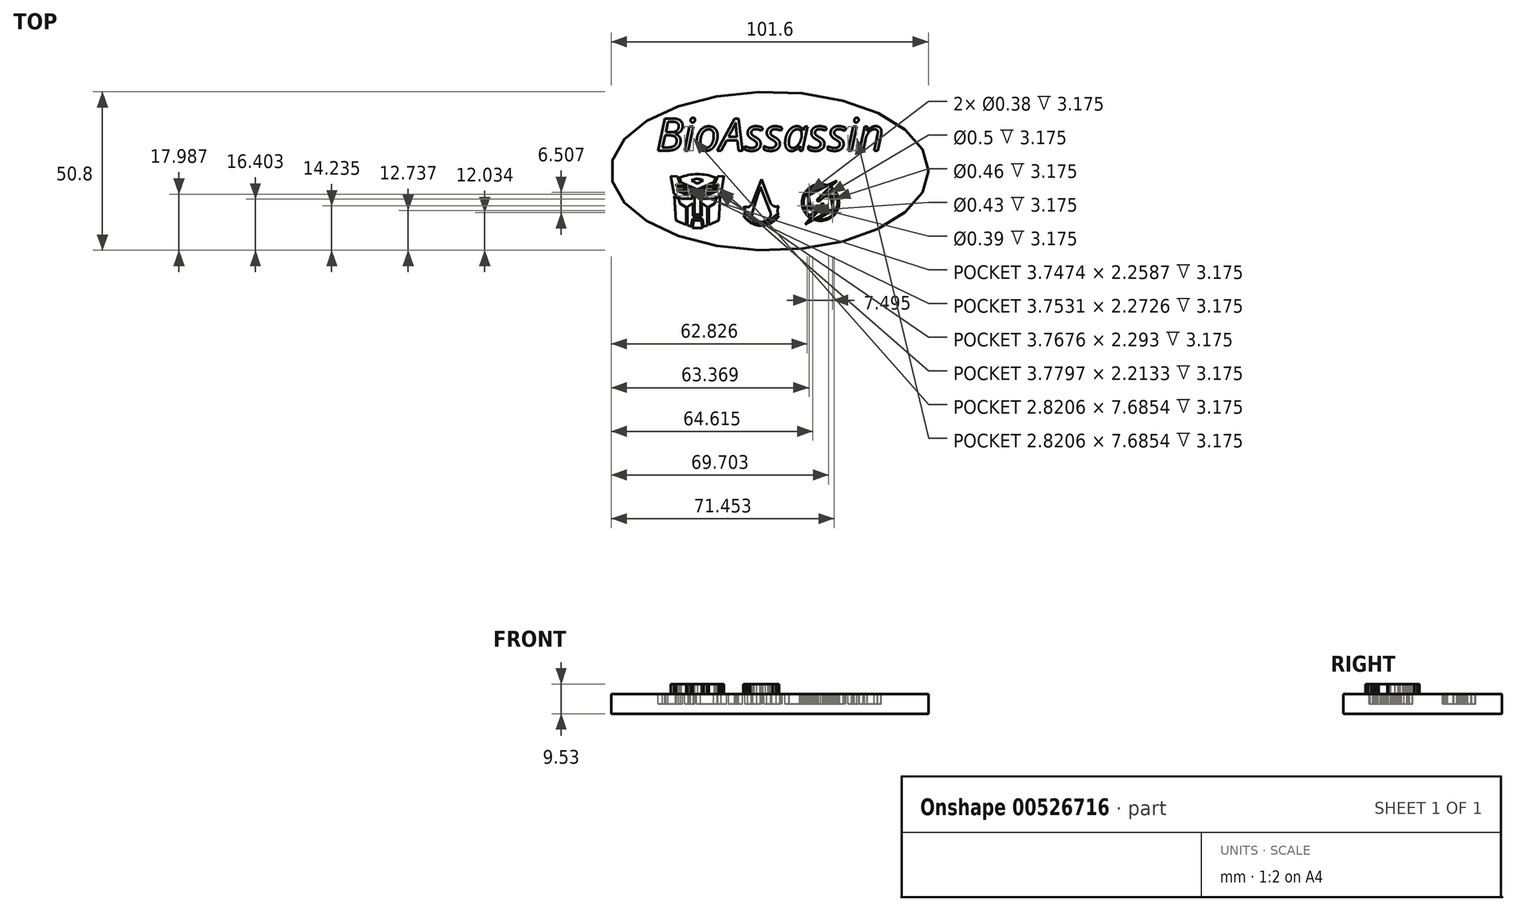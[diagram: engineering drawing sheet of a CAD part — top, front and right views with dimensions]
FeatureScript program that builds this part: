
annotation { "Feature Type Name" : "Feature", "Feature Type Description" : "" }
export const myFeature = defineFeature(function(context is Context, id is Id, definition is map)
    precondition{}
    {
        {
            var Q0;
            Q0=qCreatedBy(makeId("Top.planeOp"),FACE);
            var sketch = newSketch(context, id + "F0", { "sketchPlane" : qUnion([Q0])});
            skEllipse(sketch, "E0", {"center": v(-52.88, 26.44) * mm, "majorRadius": 50.8 * mm, "minorRadius": 25.4 * mm, "majorAxis": v(1, 0)});
            skSolve(sketch);
        }
        {
            var Q0;
            Q0=makeQuery(id+"F0.imprint","IMPRINT",FACE,{"disambiguationData":[TD([[makeQuery(id+"F0.imprint","IMPRINT",EDGE,{"derivedFrom":sQuery(id+"F0.wireOp",EDGE,"E0")}),1.0]])]});
            extrude(context, id + "F1", {"entities" : qUnion([Q0]), "depth" : 6.35 * mm, "offsetDistance" : 25.4 * mm});
        }
        {
            var Q0;
            Q0=makeQuery(id+"F1.opExtrude","CAP_FACE",FACE,{"disambiguationData":[OSD([sQuery(id+"F0.wireOp",EDGE,"E0"),sQuery(id+"F0.wireOp",EDGE,"c0c78684-51f5-4be6-9a9b-70ab7c756a0d.sketch_text.stroke-0"),sQuery(id+"F0.wireOp",EDGE,"c0c78684-51f5-4be6-9a9b-70ab7c756a0d.sketch_text.stroke-1"),sQuery(id+"F0.wireOp",EDGE,"c0c78684-51f5-4be6-9a9b-70ab7c756a0d.sketch_text.stroke-2"),sQuery(id+"F0.wireOp",EDGE,"c0c78684-51f5-4be6-9a9b-70ab7c756a0d.sketch_text.stroke-3"),sQuery(id+"F0.wireOp",EDGE,"c0c78684-51f5-4be6-9a9b-70ab7c756a0d.sketch_text.stroke-4"),sQuery(id+"F0.wireOp",EDGE,"c0c78684-51f5-4be6-9a9b-70ab7c756a0d.sketch_text.stroke-5"),sQuery(id+"F0.wireOp",EDGE,"c0c78684-51f5-4be6-9a9b-70ab7c756a0d.sketch_text.stroke-6"),sQuery(id+"F0.wireOp",EDGE,"c0c78684-51f5-4be6-9a9b-70ab7c756a0d.sketch_text.stroke-7"),sQuery(id+"F0.wireOp",EDGE,"c0c78684-51f5-4be6-9a9b-70ab7c756a0d.sketch_text.stroke-8"),sQuery(id+"F0.wireOp",EDGE,"c0c78684-51f5-4be6-9a9b-70ab7c756a0d.sketch_text.stroke-9"),sQuery(id+"F0.wireOp",EDGE,"c0c78684-51f5-4be6-9a9b-70ab7c756a0d.sketch_text.stroke-10"),sQuery(id+"F0.wireOp",EDGE,"c0c78684-51f5-4be6-9a9b-70ab7c756a0d.sketch_text.stroke-25"),sQuery(id+"F0.wireOp",EDGE,"c0c78684-51f5-4be6-9a9b-70ab7c756a0d.sketch_text.stroke-26"),sQuery(id+"F0.wireOp",EDGE,"c0c78684-51f5-4be6-9a9b-70ab7c756a0d.sketch_text.stroke-27"),sQuery(id+"F0.wireOp",EDGE,"c0c78684-51f5-4be6-9a9b-70ab7c756a0d.sketch_text.stroke-28"),sQuery(id+"F0.wireOp",EDGE,"c0c78684-51f5-4be6-9a9b-70ab7c756a0d.sketch_text.stroke-29"),sQuery(id+"F0.wireOp",EDGE,"c0c78684-51f5-4be6-9a9b-70ab7c756a0d.sketch_text.stroke-30"),sQuery(id+"F0.wireOp",EDGE,"c0c78684-51f5-4be6-9a9b-70ab7c756a0d.sketch_text.stroke-31"),sQuery(id+"F0.wireOp",EDGE,"c0c78684-51f5-4be6-9a9b-70ab7c756a0d.sketch_text.stroke-32"),sQuery(id+"F0.wireOp",EDGE,"c0c78684-51f5-4be6-9a9b-70ab7c756a0d.sketch_text.stroke-33"),sQuery(id+"F0.wireOp",EDGE,"c0c78684-51f5-4be6-9a9b-70ab7c756a0d.sketch_text.stroke-34"),sQuery(id+"F0.wireOp",EDGE,"c0c78684-51f5-4be6-9a9b-70ab7c756a0d.sketch_text.stroke-35"),sQuery(id+"F0.wireOp",EDGE,"c0c78684-51f5-4be6-9a9b-70ab7c756a0d.sketch_text.stroke-36"),sQuery(id+"F0.wireOp",EDGE,"c0c78684-51f5-4be6-9a9b-70ab7c756a0d.sketch_text.stroke-37"),sQuery(id+"F0.wireOp",EDGE,"c0c78684-51f5-4be6-9a9b-70ab7c756a0d.sketch_text.stroke-38"),sQuery(id+"F0.wireOp",EDGE,"c0c78684-51f5-4be6-9a9b-70ab7c756a0d.sketch_text.stroke-39"),sQuery(id+"F0.wireOp",EDGE,"c0c78684-51f5-4be6-9a9b-70ab7c756a0d.sketch_text.stroke-40"),sQuery(id+"F0.wireOp",EDGE,"c0c78684-51f5-4be6-9a9b-70ab7c756a0d.sketch_text.stroke-41"),sQuery(id+"F0.wireOp",EDGE,"c0c78684-51f5-4be6-9a9b-70ab7c756a0d.sketch_text.stroke-42"),sQuery(id+"F0.wireOp",EDGE,"c0c78684-51f5-4be6-9a9b-70ab7c756a0d.sketch_text.stroke-43"),sQuery(id+"F0.wireOp",EDGE,"c0c78684-51f5-4be6-9a9b-70ab7c756a0d.sketch_text.stroke-44"),sQuery(id+"F0.wireOp",EDGE,"c0c78684-51f5-4be6-9a9b-70ab7c756a0d.sketch_text.stroke-45"),sQuery(id+"F0.wireOp",EDGE,"c0c78684-51f5-4be6-9a9b-70ab7c756a0d.sketch_text.stroke-56"),sQuery(id+"F0.wireOp",EDGE,"c0c78684-51f5-4be6-9a9b-70ab7c756a0d.sketch_text.stroke-57"),sQuery(id+"F0.wireOp",EDGE,"c0c78684-51f5-4be6-9a9b-70ab7c756a0d.sketch_text.stroke-58"),sQuery(id+"F0.wireOp",EDGE,"c0c78684-51f5-4be6-9a9b-70ab7c756a0d.sketch_text.stroke-59"),sQuery(id+"F0.wireOp",EDGE,"c0c78684-51f5-4be6-9a9b-70ab7c756a0d.sketch_text.stroke-60"),sQuery(id+"F0.wireOp",EDGE,"c0c78684-51f5-4be6-9a9b-70ab7c756a0d.sketch_text.stroke-61"),sQuery(id+"F0.wireOp",EDGE,"c0c78684-51f5-4be6-9a9b-70ab7c756a0d.sketch_text.stroke-62"),sQuery(id+"F0.wireOp",EDGE,"c0c78684-51f5-4be6-9a9b-70ab7c756a0d.sketch_text.stroke-63"),sQuery(id+"F0.wireOp",EDGE,"c0c78684-51f5-4be6-9a9b-70ab7c756a0d.sketch_text.stroke-69"),sQuery(id+"F0.wireOp",EDGE,"c0c78684-51f5-4be6-9a9b-70ab7c756a0d.sketch_text.stroke-70"),sQuery(id+"F0.wireOp",EDGE,"c0c78684-51f5-4be6-9a9b-70ab7c756a0d.sketch_text.stroke-71"),sQuery(id+"F0.wireOp",EDGE,"c0c78684-51f5-4be6-9a9b-70ab7c756a0d.sketch_text.stroke-72"),sQuery(id+"F0.wireOp",EDGE,"c0c78684-51f5-4be6-9a9b-70ab7c756a0d.sketch_text.stroke-73"),sQuery(id+"F0.wireOp",EDGE,"c0c78684-51f5-4be6-9a9b-70ab7c756a0d.sketch_text.stroke-74"),sQuery(id+"F0.wireOp",EDGE,"c0c78684-51f5-4be6-9a9b-70ab7c756a0d.sketch_text.stroke-75"),sQuery(id+"F0.wireOp",EDGE,"c0c78684-51f5-4be6-9a9b-70ab7c756a0d.sketch_text.stroke-76"),sQuery(id+"F0.wireOp",EDGE,"c0c78684-51f5-4be6-9a9b-70ab7c756a0d.sketch_text.stroke-77"),sQuery(id+"F0.wireOp",EDGE,"c0c78684-51f5-4be6-9a9b-70ab7c756a0d.sketch_text.stroke-78"),sQuery(id+"F0.wireOp",EDGE,"c0c78684-51f5-4be6-9a9b-70ab7c756a0d.sketch_text.stroke-79"),sQuery(id+"F0.wireOp",EDGE,"c0c78684-51f5-4be6-9a9b-70ab7c756a0d.sketch_text.stroke-80"),sQuery(id+"F0.wireOp",EDGE,"c0c78684-51f5-4be6-9a9b-70ab7c756a0d.sketch_text.stroke-81"),sQuery(id+"F0.wireOp",EDGE,"c0c78684-51f5-4be6-9a9b-70ab7c756a0d.sketch_text.stroke-82"),sQuery(id+"F0.wireOp",EDGE,"c0c78684-51f5-4be6-9a9b-70ab7c756a0d.sketch_text.stroke-83"),sQuery(id+"F0.wireOp",EDGE,"c0c78684-51f5-4be6-9a9b-70ab7c756a0d.sketch_text.stroke-84"),sQuery(id+"F0.wireOp",EDGE,"c0c78684-51f5-4be6-9a9b-70ab7c756a0d.sketch_text.stroke-85"),sQuery(id+"F0.wireOp",EDGE,"c0c78684-51f5-4be6-9a9b-70ab7c756a0d.sketch_text.stroke-86"),sQuery(id+"F0.wireOp",EDGE,"c0c78684-51f5-4be6-9a9b-70ab7c756a0d.sketch_text.stroke-87"),sQuery(id+"F0.wireOp",EDGE,"c0c78684-51f5-4be6-9a9b-70ab7c756a0d.sketch_text.stroke-88"),sQuery(id+"F0.wireOp",EDGE,"c0c78684-51f5-4be6-9a9b-70ab7c756a0d.sketch_text.stroke-89"),sQuery(id+"F0.wireOp",EDGE,"c0c78684-51f5-4be6-9a9b-70ab7c756a0d.sketch_text.stroke-90"),sQuery(id+"F0.wireOp",EDGE,"c0c78684-51f5-4be6-9a9b-70ab7c756a0d.sketch_text.stroke-91"),sQuery(id+"F0.wireOp",EDGE,"c0c78684-51f5-4be6-9a9b-70ab7c756a0d.sketch_text.stroke-92"),sQuery(id+"F0.wireOp",EDGE,"c0c78684-51f5-4be6-9a9b-70ab7c756a0d.sketch_text.stroke-93"),sQuery(id+"F0.wireOp",EDGE,"c0c78684-51f5-4be6-9a9b-70ab7c756a0d.sketch_text.stroke-94"),sQuery(id+"F0.wireOp",EDGE,"c0c78684-51f5-4be6-9a9b-70ab7c756a0d.sketch_text.stroke-95"),sQuery(id+"F0.wireOp",EDGE,"c0c78684-51f5-4be6-9a9b-70ab7c756a0d.sketch_text.stroke-96"),sQuery(id+"F0.wireOp",EDGE,"c0c78684-51f5-4be6-9a9b-70ab7c756a0d.sketch_text.stroke-97"),sQuery(id+"F0.wireOp",EDGE,"c0c78684-51f5-4be6-9a9b-70ab7c756a0d.sketch_text.stroke-98"),sQuery(id+"F0.wireOp",EDGE,"c0c78684-51f5-4be6-9a9b-70ab7c756a0d.sketch_text.stroke-99"),sQuery(id+"F0.wireOp",EDGE,"c0c78684-51f5-4be6-9a9b-70ab7c756a0d.sketch_text.stroke-100"),sQuery(id+"F0.wireOp",EDGE,"c0c78684-51f5-4be6-9a9b-70ab7c756a0d.sketch_text.stroke-101"),sQuery(id+"F0.wireOp",EDGE,"c0c78684-51f5-4be6-9a9b-70ab7c756a0d.sketch_text.stroke-102"),sQuery(id+"F0.wireOp",EDGE,"c0c78684-51f5-4be6-9a9b-70ab7c756a0d.sketch_text.stroke-103"),sQuery(id+"F0.wireOp",EDGE,"c0c78684-51f5-4be6-9a9b-70ab7c756a0d.sketch_text.stroke-104"),sQuery(id+"F0.wireOp",EDGE,"c0c78684-51f5-4be6-9a9b-70ab7c756a0d.sketch_text.stroke-105"),sQuery(id+"F0.wireOp",EDGE,"c0c78684-51f5-4be6-9a9b-70ab7c756a0d.sketch_text.stroke-106"),sQuery(id+"F0.wireOp",EDGE,"c0c78684-51f5-4be6-9a9b-70ab7c756a0d.sketch_text.stroke-107"),sQuery(id+"F0.wireOp",EDGE,"c0c78684-51f5-4be6-9a9b-70ab7c756a0d.sketch_text.stroke-108"),sQuery(id+"F0.wireOp",EDGE,"c0c78684-51f5-4be6-9a9b-70ab7c756a0d.sketch_text.stroke-109"),sQuery(id+"F0.wireOp",EDGE,"c0c78684-51f5-4be6-9a9b-70ab7c756a0d.sketch_text.stroke-110"),sQuery(id+"F0.wireOp",EDGE,"c0c78684-51f5-4be6-9a9b-70ab7c756a0d.sketch_text.stroke-111"),sQuery(id+"F0.wireOp",EDGE,"c0c78684-51f5-4be6-9a9b-70ab7c756a0d.sketch_text.stroke-112"),sQuery(id+"F0.wireOp",EDGE,"c0c78684-51f5-4be6-9a9b-70ab7c756a0d.sketch_text.stroke-113"),sQuery(id+"F0.wireOp",EDGE,"c0c78684-51f5-4be6-9a9b-70ab7c756a0d.sketch_text.stroke-114"),sQuery(id+"F0.wireOp",EDGE,"c0c78684-51f5-4be6-9a9b-70ab7c756a0d.sketch_text.stroke-115"),sQuery(id+"F0.wireOp",EDGE,"c0c78684-51f5-4be6-9a9b-70ab7c756a0d.sketch_text.stroke-116"),sQuery(id+"F0.wireOp",EDGE,"c0c78684-51f5-4be6-9a9b-70ab7c756a0d.sketch_text.stroke-117"),sQuery(id+"F0.wireOp",EDGE,"c0c78684-51f5-4be6-9a9b-70ab7c756a0d.sketch_text.stroke-118"),sQuery(id+"F0.wireOp",EDGE,"c0c78684-51f5-4be6-9a9b-70ab7c756a0d.sketch_text.stroke-119"),sQuery(id+"F0.wireOp",EDGE,"c0c78684-51f5-4be6-9a9b-70ab7c756a0d.sketch_text.stroke-120"),sQuery(id+"F0.wireOp",EDGE,"c0c78684-51f5-4be6-9a9b-70ab7c756a0d.sketch_text.stroke-121"),sQuery(id+"F0.wireOp",EDGE,"c0c78684-51f5-4be6-9a9b-70ab7c756a0d.sketch_text.stroke-122"),sQuery(id+"F0.wireOp",EDGE,"c0c78684-51f5-4be6-9a9b-70ab7c756a0d.sketch_text.stroke-123"),sQuery(id+"F0.wireOp",EDGE,"c0c78684-51f5-4be6-9a9b-70ab7c756a0d.sketch_text.stroke-124"),sQuery(id+"F0.wireOp",EDGE,"c0c78684-51f5-4be6-9a9b-70ab7c756a0d.sketch_text.stroke-125"),sQuery(id+"F0.wireOp",EDGE,"c0c78684-51f5-4be6-9a9b-70ab7c756a0d.sketch_text.stroke-126"),sQuery(id+"F0.wireOp",EDGE,"c0c78684-51f5-4be6-9a9b-70ab7c756a0d.sketch_text.stroke-127"),sQuery(id+"F0.wireOp",EDGE,"c0c78684-51f5-4be6-9a9b-70ab7c756a0d.sketch_text.stroke-128"),sQuery(id+"F0.wireOp",EDGE,"c0c78684-51f5-4be6-9a9b-70ab7c756a0d.sketch_text.stroke-129"),sQuery(id+"F0.wireOp",EDGE,"c0c78684-51f5-4be6-9a9b-70ab7c756a0d.sketch_text.stroke-130"),sQuery(id+"F0.wireOp",EDGE,"c0c78684-51f5-4be6-9a9b-70ab7c756a0d.sketch_text.stroke-131"),sQuery(id+"F0.wireOp",EDGE,"c0c78684-51f5-4be6-9a9b-70ab7c756a0d.sketch_text.stroke-132"),sQuery(id+"F0.wireOp",EDGE,"c0c78684-51f5-4be6-9a9b-70ab7c756a0d.sketch_text.stroke-133"),sQuery(id+"F0.wireOp",EDGE,"c0c78684-51f5-4be6-9a9b-70ab7c756a0d.sketch_text.stroke-144"),sQuery(id+"F0.wireOp",EDGE,"c0c78684-51f5-4be6-9a9b-70ab7c756a0d.sketch_text.stroke-145"),sQuery(id+"F0.wireOp",EDGE,"c0c78684-51f5-4be6-9a9b-70ab7c756a0d.sketch_text.stroke-146"),sQuery(id+"F0.wireOp",EDGE,"c0c78684-51f5-4be6-9a9b-70ab7c756a0d.sketch_text.stroke-147"),sQuery(id+"F0.wireOp",EDGE,"c0c78684-51f5-4be6-9a9b-70ab7c756a0d.sketch_text.stroke-148"),sQuery(id+"F0.wireOp",EDGE,"c0c78684-51f5-4be6-9a9b-70ab7c756a0d.sketch_text.stroke-149"),sQuery(id+"F0.wireOp",EDGE,"c0c78684-51f5-4be6-9a9b-70ab7c756a0d.sketch_text.stroke-150"),sQuery(id+"F0.wireOp",EDGE,"c0c78684-51f5-4be6-9a9b-70ab7c756a0d.sketch_text.stroke-151"),sQuery(id+"F0.wireOp",EDGE,"c0c78684-51f5-4be6-9a9b-70ab7c756a0d.sketch_text.stroke-152"),sQuery(id+"F0.wireOp",EDGE,"c0c78684-51f5-4be6-9a9b-70ab7c756a0d.sketch_text.stroke-153"),sQuery(id+"F0.wireOp",EDGE,"c0c78684-51f5-4be6-9a9b-70ab7c756a0d.sketch_text.stroke-154"),sQuery(id+"F0.wireOp",EDGE,"c0c78684-51f5-4be6-9a9b-70ab7c756a0d.sketch_text.stroke-155"),sQuery(id+"F0.wireOp",EDGE,"c0c78684-51f5-4be6-9a9b-70ab7c756a0d.sketch_text.stroke-156"),sQuery(id+"F0.wireOp",EDGE,"c0c78684-51f5-4be6-9a9b-70ab7c756a0d.sketch_text.stroke-157"),sQuery(id+"F0.wireOp",EDGE,"c0c78684-51f5-4be6-9a9b-70ab7c756a0d.sketch_text.stroke-158"),sQuery(id+"F0.wireOp",EDGE,"c0c78684-51f5-4be6-9a9b-70ab7c756a0d.sketch_text.stroke-159"),sQuery(id+"F0.wireOp",EDGE,"c0c78684-51f5-4be6-9a9b-70ab7c756a0d.sketch_text.stroke-160"),sQuery(id+"F0.wireOp",EDGE,"c0c78684-51f5-4be6-9a9b-70ab7c756a0d.sketch_text.stroke-161"),sQuery(id+"F0.wireOp",EDGE,"c0c78684-51f5-4be6-9a9b-70ab7c756a0d.sketch_text.stroke-162"),sQuery(id+"F0.wireOp",EDGE,"c0c78684-51f5-4be6-9a9b-70ab7c756a0d.sketch_text.stroke-163"),sQuery(id+"F0.wireOp",EDGE,"c0c78684-51f5-4be6-9a9b-70ab7c756a0d.sketch_text.stroke-164"),sQuery(id+"F0.wireOp",EDGE,"c0c78684-51f5-4be6-9a9b-70ab7c756a0d.sketch_text.stroke-165"),sQuery(id+"F0.wireOp",EDGE,"c0c78684-51f5-4be6-9a9b-70ab7c756a0d.sketch_text.stroke-166"),sQuery(id+"F0.wireOp",EDGE,"c0c78684-51f5-4be6-9a9b-70ab7c756a0d.sketch_text.stroke-167"),sQuery(id+"F0.wireOp",EDGE,"c0c78684-51f5-4be6-9a9b-70ab7c756a0d.sketch_text.stroke-168"),sQuery(id+"F0.wireOp",EDGE,"c0c78684-51f5-4be6-9a9b-70ab7c756a0d.sketch_text.stroke-169"),sQuery(id+"F0.wireOp",EDGE,"c0c78684-51f5-4be6-9a9b-70ab7c756a0d.sketch_text.stroke-170"),sQuery(id+"F0.wireOp",EDGE,"c0c78684-51f5-4be6-9a9b-70ab7c756a0d.sketch_text.stroke-171"),sQuery(id+"F0.wireOp",EDGE,"c0c78684-51f5-4be6-9a9b-70ab7c756a0d.sketch_text.stroke-172"),sQuery(id+"F0.wireOp",EDGE,"c0c78684-51f5-4be6-9a9b-70ab7c756a0d.sketch_text.stroke-173"),sQuery(id+"F0.wireOp",EDGE,"c0c78684-51f5-4be6-9a9b-70ab7c756a0d.sketch_text.stroke-174"),sQuery(id+"F0.wireOp",EDGE,"c0c78684-51f5-4be6-9a9b-70ab7c756a0d.sketch_text.stroke-175"),sQuery(id+"F0.wireOp",EDGE,"c0c78684-51f5-4be6-9a9b-70ab7c756a0d.sketch_text.stroke-176"),sQuery(id+"F0.wireOp",EDGE,"c0c78684-51f5-4be6-9a9b-70ab7c756a0d.sketch_text.stroke-177"),sQuery(id+"F0.wireOp",EDGE,"c0c78684-51f5-4be6-9a9b-70ab7c756a0d.sketch_text.stroke-178"),sQuery(id+"F0.wireOp",EDGE,"c0c78684-51f5-4be6-9a9b-70ab7c756a0d.sketch_text.stroke-179"),sQuery(id+"F0.wireOp",EDGE,"c0c78684-51f5-4be6-9a9b-70ab7c756a0d.sketch_text.stroke-180"),sQuery(id+"F0.wireOp",EDGE,"c0c78684-51f5-4be6-9a9b-70ab7c756a0d.sketch_text.stroke-181"),sQuery(id+"F0.wireOp",EDGE,"c0c78684-51f5-4be6-9a9b-70ab7c756a0d.sketch_text.stroke-182"),sQuery(id+"F0.wireOp",EDGE,"c0c78684-51f5-4be6-9a9b-70ab7c756a0d.sketch_text.stroke-183"),sQuery(id+"F0.wireOp",EDGE,"c0c78684-51f5-4be6-9a9b-70ab7c756a0d.sketch_text.stroke-184"),sQuery(id+"F0.wireOp",EDGE,"c0c78684-51f5-4be6-9a9b-70ab7c756a0d.sketch_text.stroke-185"),sQuery(id+"F0.wireOp",EDGE,"c0c78684-51f5-4be6-9a9b-70ab7c756a0d.sketch_text.stroke-186"),sQuery(id+"F0.wireOp",EDGE,"c0c78684-51f5-4be6-9a9b-70ab7c756a0d.sketch_text.stroke-187"),sQuery(id+"F0.wireOp",EDGE,"c0c78684-51f5-4be6-9a9b-70ab7c756a0d.sketch_text.stroke-188"),sQuery(id+"F0.wireOp",EDGE,"c0c78684-51f5-4be6-9a9b-70ab7c756a0d.sketch_text.stroke-189"),sQuery(id+"F0.wireOp",EDGE,"c0c78684-51f5-4be6-9a9b-70ab7c756a0d.sketch_text.stroke-190"),sQuery(id+"F0.wireOp",EDGE,"c0c78684-51f5-4be6-9a9b-70ab7c756a0d.sketch_text.stroke-191"),sQuery(id+"F0.wireOp",EDGE,"c0c78684-51f5-4be6-9a9b-70ab7c756a0d.sketch_text.stroke-192"),sQuery(id+"F0.wireOp",EDGE,"c0c78684-51f5-4be6-9a9b-70ab7c756a0d.sketch_text.stroke-193"),sQuery(id+"F0.wireOp",EDGE,"c0c78684-51f5-4be6-9a9b-70ab7c756a0d.sketch_text.stroke-194"),sQuery(id+"F0.wireOp",EDGE,"c0c78684-51f5-4be6-9a9b-70ab7c756a0d.sketch_text.stroke-195"),sQuery(id+"F0.wireOp",EDGE,"c0c78684-51f5-4be6-9a9b-70ab7c756a0d.sketch_text.stroke-196"),sQuery(id+"F0.wireOp",EDGE,"c0c78684-51f5-4be6-9a9b-70ab7c756a0d.sketch_text.stroke-197"),sQuery(id+"F0.wireOp",EDGE,"c0c78684-51f5-4be6-9a9b-70ab7c756a0d.sketch_text.stroke-198"),sQuery(id+"F0.wireOp",EDGE,"c0c78684-51f5-4be6-9a9b-70ab7c756a0d.sketch_text.stroke-199"),sQuery(id+"F0.wireOp",EDGE,"c0c78684-51f5-4be6-9a9b-70ab7c756a0d.sketch_text.stroke-200"),sQuery(id+"F0.wireOp",EDGE,"c0c78684-51f5-4be6-9a9b-70ab7c756a0d.sketch_text.stroke-201"),sQuery(id+"F0.wireOp",EDGE,"c0c78684-51f5-4be6-9a9b-70ab7c756a0d.sketch_text.stroke-202"),sQuery(id+"F0.wireOp",EDGE,"c0c78684-51f5-4be6-9a9b-70ab7c756a0d.sketch_text.stroke-203"),sQuery(id+"F0.wireOp",EDGE,"c0c78684-51f5-4be6-9a9b-70ab7c756a0d.sketch_text.stroke-204"),sQuery(id+"F0.wireOp",EDGE,"c0c78684-51f5-4be6-9a9b-70ab7c756a0d.sketch_text.stroke-205"),sQuery(id+"F0.wireOp",EDGE,"c0c78684-51f5-4be6-9a9b-70ab7c756a0d.sketch_text.stroke-206"),sQuery(id+"F0.wireOp",EDGE,"c0c78684-51f5-4be6-9a9b-70ab7c756a0d.sketch_text.stroke-207"),sQuery(id+"F0.wireOp",EDGE,"c0c78684-51f5-4be6-9a9b-70ab7c756a0d.sketch_text.stroke-208"),sQuery(id+"F0.wireOp",EDGE,"c0c78684-51f5-4be6-9a9b-70ab7c756a0d.sketch_text.stroke-209"),sQuery(id+"F0.wireOp",EDGE,"c0c78684-51f5-4be6-9a9b-70ab7c756a0d.sketch_text.stroke-210"),sQuery(id+"F0.wireOp",EDGE,"c0c78684-51f5-4be6-9a9b-70ab7c756a0d.sketch_text.stroke-211"),sQuery(id+"F0.wireOp",EDGE,"c0c78684-51f5-4be6-9a9b-70ab7c756a0d.sketch_text.stroke-212"),sQuery(id+"F0.wireOp",EDGE,"c0c78684-51f5-4be6-9a9b-70ab7c756a0d.sketch_text.stroke-213"),sQuery(id+"F0.wireOp",EDGE,"c0c78684-51f5-4be6-9a9b-70ab7c756a0d.sketch_text.stroke-214"),sQuery(id+"F0.wireOp",EDGE,"c0c78684-51f5-4be6-9a9b-70ab7c756a0d.sketch_text.stroke-215"),sQuery(id+"F0.wireOp",EDGE,"c0c78684-51f5-4be6-9a9b-70ab7c756a0d.sketch_text.stroke-216"),sQuery(id+"F0.wireOp",EDGE,"c0c78684-51f5-4be6-9a9b-70ab7c756a0d.sketch_text.stroke-217"),sQuery(id+"F0.wireOp",EDGE,"c0c78684-51f5-4be6-9a9b-70ab7c756a0d.sketch_text.stroke-218"),sQuery(id+"F0.wireOp",EDGE,"c0c78684-51f5-4be6-9a9b-70ab7c756a0d.sketch_text.stroke-219"),sQuery(id+"F0.wireOp",EDGE,"c0c78684-51f5-4be6-9a9b-70ab7c756a0d.sketch_text.stroke-220"),sQuery(id+"F0.wireOp",EDGE,"c0c78684-51f5-4be6-9a9b-70ab7c756a0d.sketch_text.stroke-221"),sQuery(id+"F0.wireOp",EDGE,"c0c78684-51f5-4be6-9a9b-70ab7c756a0d.sketch_text.stroke-222"),sQuery(id+"F0.wireOp",EDGE,"c0c78684-51f5-4be6-9a9b-70ab7c756a0d.sketch_text.stroke-223"),sQuery(id+"F0.wireOp",EDGE,"c0c78684-51f5-4be6-9a9b-70ab7c756a0d.sketch_text.stroke-224")])],"isStart":false});
            var sketch = newSketch(context, id + "F2", { "sketchPlane" : qUnion([Q0])});
            skLineSegment(sketch, "E1", {"start": v(-78.93, 19.1) * mm, "end": v(-78.82, 18.46) * mm});
            skLineSegment(sketch, "E2", {"start": v(-78.82, 18.46) * mm, "end": v(-82.45, 20.08) * mm});
            skLineSegment(sketch, "E3", {"start": v(-82.45, 20.08) * mm, "end": v(-82.56, 20.72) * mm});
            skLineSegment(sketch, "E4", {"start": v(-82.56, 20.72) * mm, "end": v(-78.93, 19.1) * mm});
            skLineSegment(sketch, "E5", {"start": v(-73.12, 19.1) * mm, "end": v(-73.25, 18.4) * mm});
            skLineSegment(sketch, "E6", {"start": v(-73.25, 18.4) * mm, "end": v(-69.6, 20.08) * mm});
            skLineSegment(sketch, "E7", {"start": v(-69.6, 20.08) * mm, "end": v(-69.48, 20.7) * mm});
            skLineSegment(sketch, "E8", {"start": v(-69.48, 20.7) * mm, "end": v(-73.12, 19.1) * mm});
            skLineSegment(sketch, "E9", {"start": v(-72.89, 20.55) * mm, "end": v(-72.98, 19.97) * mm});
            skLineSegment(sketch, "E10", {"start": v(-72.98, 19.97) * mm, "end": v(-69.33, 21.6) * mm});
            skLineSegment(sketch, "E11", {"start": v(-69.33, 21.6) * mm, "end": v(-69.2, 22.18) * mm});
            skLineSegment(sketch, "E12", {"start": v(-69.2, 22.18) * mm, "end": v(-72.89, 20.55) * mm});
            skLineSegment(sketch, "E13", {"start": v(-82.85, 22.23) * mm, "end": v(-82.75, 21.59) * mm});
            skLineSegment(sketch, "E14", {"start": v(-82.75, 21.59) * mm, "end": v(-79.1, 19.95) * mm});
            skLineSegment(sketch, "E15", {"start": v(-79.1, 19.95) * mm, "end": v(-79.2, 20.56) * mm});
            skLineSegment(sketch, "E16", {"start": v(-79.2, 20.56) * mm, "end": v(-82.85, 22.23) * mm});
            skLineSegment(sketch, "E17", {"start": v(-84.54, 24.8) * mm, "end": v(-82.41, 24.72) * mm});
            skLineSegment(sketch, "E18", {"start": v(-82.41, 24.72) * mm, "end": v(-81.67, 22.48) * mm});
            skLineSegment(sketch, "E19", {"start": v(-81.67, 22.48) * mm, "end": v(-78.19, 20.98) * mm});
            skLineSegment(sketch, "E20", {"start": v(-78.19, 20.98) * mm, "end": v(-77.63, 17.52) * mm});
            skLineSegment(sketch, "E21", {"start": v(-77.63, 17.52) * mm, "end": v(-81.27, 17.52) * mm});
            skLineSegment(sketch, "E22", {"start": v(-81.27, 17.52) * mm, "end": v(-83.56, 19.25) * mm});
            skLineSegment(sketch, "E23", {"start": v(-83.56, 19.25) * mm, "end": v(-84.54, 24.8) * mm});
            skLineSegment(sketch, "E24", {"start": v(-67.55, 24.8) * mm, "end": v(-69.64, 24.72) * mm});
            skLineSegment(sketch, "E25", {"start": v(-69.64, 24.72) * mm, "end": v(-70.41, 22.5) * mm});
            skLineSegment(sketch, "E26", {"start": v(-70.41, 22.5) * mm, "end": v(-73.93, 20.94) * mm});
            skLineSegment(sketch, "E27", {"start": v(-73.93, 20.94) * mm, "end": v(-74.42, 17.52) * mm});
            skLineSegment(sketch, "E28", {"start": v(-74.42, 17.52) * mm, "end": v(-70.78, 17.52) * mm});
            skLineSegment(sketch, "E29", {"start": v(-70.78, 17.52) * mm, "end": v(-68.49, 19.25) * mm});
            skLineSegment(sketch, "E30", {"start": v(-68.49, 19.25) * mm, "end": v(-67.55, 24.8) * mm});
            skLineSegment(sketch, "E31", {"start": v(-83.38, 18.48) * mm, "end": v(-82.1, 17.58) * mm});
            skLineSegment(sketch, "E32", {"start": v(-82.1, 17.58) * mm, "end": v(-81.67, 16) * mm});
            skLineSegment(sketch, "E33", {"start": v(-81.67, 16) * mm, "end": v(-79.66, 14.83) * mm});
            skLineSegment(sketch, "E34", {"start": v(-79.66, 14.83) * mm, "end": v(-79.66, 9.23) * mm});
            skLineSegment(sketch, "E35", {"start": v(-79.66, 9.23) * mm, "end": v(-82.89, 10.57) * mm});
            skLineSegment(sketch, "E36", {"start": v(-82.89, 10.57) * mm, "end": v(-83.38, 18.48) * mm});
            skLineSegment(sketch, "E37", {"start": v(-68.71, 18.55) * mm, "end": v(-70, 17.58) * mm});
            skLineSegment(sketch, "E38", {"start": v(-70, 17.58) * mm, "end": v(-70.44, 16) * mm});
            skLineSegment(sketch, "E39", {"start": v(-70.44, 16) * mm, "end": v(-72.42, 14.9) * mm});
            skLineSegment(sketch, "E40", {"start": v(-72.42, 14.9) * mm, "end": v(-72.42, 9.23) * mm});
            skLineSegment(sketch, "E41", {"start": v(-72.42, 9.23) * mm, "end": v(-69.17, 10.57) * mm});
            skLineSegment(sketch, "E42", {"start": v(-69.17, 10.57) * mm, "end": v(-68.71, 18.55) * mm});
            skLineSegment(sketch, "E43", {"start": v(-78.05, 8.61) * mm, "end": v(-79.2, 9.1) * mm});
            skLineSegment(sketch, "E44", {"start": v(-79.2, 9.1) * mm, "end": v(-79.2, 14.9) * mm});
            skLineSegment(sketch, "E45", {"start": v(-79.2, 14.9) * mm, "end": v(-77.5, 16.18) * mm});
            skLineSegment(sketch, "E46", {"start": v(-77.5, 16.18) * mm, "end": v(-77.5, 11.94) * mm});
            skLineSegment(sketch, "E47", {"start": v(-77.5, 11.94) * mm, "end": v(-74.62, 11.94) * mm});
            skLineSegment(sketch, "E48", {"start": v(-74.62, 11.94) * mm, "end": v(-74.62, 16.2) * mm});
            skLineSegment(sketch, "E49", {"start": v(-74.62, 16.2) * mm, "end": v(-72.88, 14.9) * mm});
            skLineSegment(sketch, "E50", {"start": v(-72.88, 14.9) * mm, "end": v(-72.88, 8.98) * mm});
            skLineSegment(sketch, "E51", {"start": v(-72.88, 8.98) * mm, "end": v(-73.99, 8.64) * mm});
            skLineSegment(sketch, "E52", {"start": v(-73.99, 8.64) * mm, "end": v(-74.43, 11.07) * mm});
            skLineSegment(sketch, "E53", {"start": v(-74.43, 11.07) * mm, "end": v(-77.63, 11.07) * mm});
            skLineSegment(sketch, "E54", {"start": v(-77.63, 11.07) * mm, "end": v(-78.05, 8.61) * mm});
            skLineSegment(sketch, "E55", {"start": v(-75.11, 12.45) * mm, "end": v(-77.01, 12.45) * mm});
            skLineSegment(sketch, "E56", {"start": v(-77.01, 12.45) * mm, "end": v(-77.01, 17.42) * mm});
            skLineSegment(sketch, "E57", {"start": v(-77.01, 17.42) * mm, "end": v(-77.63, 20.68) * mm});
            skLineSegment(sketch, "E58", {"start": v(-77.63, 20.68) * mm, "end": v(-76.04, 20.01) * mm});
            skLineSegment(sketch, "E59", {"start": v(-76.04, 20.01) * mm, "end": v(-74.5, 20.68) * mm});
            skLineSegment(sketch, "E60", {"start": v(-74.5, 20.68) * mm, "end": v(-75.07, 17.4) * mm});
            skLineSegment(sketch, "E61", {"start": v(-75.07, 17.4) * mm, "end": v(-75.11, 12.45) * mm});
            skLineSegment(sketch, "E62", {"start": v(-74.43, 8.2) * mm, "end": v(-77.63, 8.2) * mm});
            skLineSegment(sketch, "E63", {"start": v(-77.63, 8.2) * mm, "end": v(-77.23, 10.57) * mm});
            skLineSegment(sketch, "E64", {"start": v(-77.23, 10.57) * mm, "end": v(-74.81, 10.57) * mm});
            skLineSegment(sketch, "E65", {"start": v(-74.81, 10.57) * mm, "end": v(-74.43, 8.2) * mm});
            skLineSegment(sketch, "E66", {"start": v(-76.04, 20.55) * mm, "end": v(-81.28, 22.8) * mm});
            skLineSegment(sketch, "E67", {"start": v(-81.28, 22.8) * mm, "end": v(-81.77, 24.29) * mm});
            skLineSegment(sketch, "E68", {"start": v(-76.04, 20.55) * mm, "end": v(-70.72, 22.91) * mm});
            skLineSegment(sketch, "E69", {"start": v(-70.72, 22.91) * mm, "end": v(-70.29, 24.34) * mm});
            skLineSegment(sketch, "E70", {"start": v(-76.05, 22.34) * mm, "end": v(-77.94, 23.43) * mm});
            skLineSegment(sketch, "E71", {"start": v(-76.05, 22.34) * mm, "end": v(-74.15, 23.4) * mm});
            skArc(sketch, "E72", {"start": v(-74.15, 23.4) * mm, "mid": v(-76.04, 23.88) * mm, "end": v(-77.94, 23.43) * mm});
            skArc(sketch, "E73", {"start": v(-70.29, 24.34) * mm, "mid": v(-76.03, 25.43) * mm, "end": v(-81.77, 24.29) * mm});
            skSolve(sketch);
        }
        {
            var Q0;
            Q0=makeQuery(id+"F2.imprint","IMPRINT",FACE,{"disambiguationData":[TD([[makeQuery(id+"F2.imprint","IMPRINT",EDGE,{"derivedFrom":sQuery(id+"F2.wireOp",EDGE,"E1")}),1.0]])]});
            var Q1;
            Q1=makeQuery(id+"F2.imprint","IMPRINT",FACE,{"disambiguationData":[TD([[makeQuery(id+"F2.imprint","IMPRINT",EDGE,{"derivedFrom":sQuery(id+"F2.wireOp",EDGE,"E66")}),-1.0]])]});
            var Q2;
            Q2=makeQuery(id+"F2.imprint","IMPRINT",FACE,{"disambiguationData":[TD([[makeQuery(id+"F2.imprint","IMPRINT",EDGE,{"derivedFrom":sQuery(id+"F2.wireOp",EDGE,"E5")}),-1.0]])]});
            var Q3;
            Q3=makeQuery(id+"F2.imprint","IMPRINT",FACE,{"disambiguationData":[TD([[makeQuery(id+"F2.imprint","IMPRINT",EDGE,{"derivedFrom":sQuery(id+"F2.wireOp",EDGE,"E55")}),-1.0]])]});
            var Q4;
            Q4=makeQuery(id+"F2.imprint","IMPRINT",FACE,{"disambiguationData":[TD([[makeQuery(id+"F2.imprint","IMPRINT",EDGE,{"derivedFrom":sQuery(id+"F2.wireOp",EDGE,"E37")}),1.0]])]});
            var Q5;
            Q5=makeQuery(id+"F2.imprint","IMPRINT",FACE,{"disambiguationData":[TD([[makeQuery(id+"F2.imprint","IMPRINT",EDGE,{"derivedFrom":sQuery(id+"F2.wireOp",EDGE,"E43")}),-1.0]])]});
            var Q6;
            Q6=makeQuery(id+"F2.imprint","IMPRINT",FACE,{"disambiguationData":[TD([[makeQuery(id+"F2.imprint","IMPRINT",EDGE,{"derivedFrom":sQuery(id+"F2.wireOp",EDGE,"E31")}),-1.0]])]});
            var Q7;
            Q7=makeQuery(id+"F2.imprint","IMPRINT",FACE,{"disambiguationData":[TD([[makeQuery(id+"F2.imprint","IMPRINT",EDGE,{"derivedFrom":sQuery(id+"F2.wireOp",EDGE,"E62")}),-1.0]])]});
            extrude(context, id + "F3", {"entities" : qUnion([Q0, Q1, Q2, Q3, Q4, Q5, Q6, Q7]), "operationType" : NewBodyOperationType.ADD, "depth" : 3.17 * mm, "offsetDistance" : 25.4 * mm});
        }
        {
            var Q0;
            {var subQ0=sQuery(id+"F0.wireOp",EDGE,"E0");Q0=makeQuery(id+"F3.boolean.opBoolean","SPLIT",FACE,{"disambiguationData":[TD([makeQuery(id+"F1.opExtrude","SWEPT_FACE",FACE,{"disambiguationData":[OSD([subQ0])]})])],"derivedFrom":makeQuery(id+"F1.opExtrude","CAP_FACE",FACE,{"disambiguationData":[OSD([subQ0])],"isStart":false})});}
            var sketch = newSketch(context, id + "F4", { "sketchPlane" : qUnion([Q0])});
            skText(sketch, "E74", { "text": "BioAssassin\n", "fontName": "OpenSans-Italic.ttf"});
            const initialGuessF4  = {"E74": [-0.0892, 0.03298, 1, 0, 0.01034]};
            skSetInitialGuess(sketch, initialGuessF4);
            skSolve(sketch);
        }
        {
            var Q0;
            Q0 = qSketchRegion(id + "F4", true);
            extrude(context, id + "F5", {"entities" : qUnion([Q0]), "operationType" : NewBodyOperationType.REMOVE, "oppositeDirection" : true, "depth" : 3.17 * mm, "offsetDistance" : 25.4 * mm});
        }
        {
            var Q0;
            {var subQ47=sQuery(id+"F0.wireOp",EDGE,"E0");var subQ48=makeQuery(id+"F1.opExtrude","SWEPT_FACE",FACE,{"disambiguationData":[OSD([subQ47])]});Q0=makeQuery(id+"F5.boolean.opBoolean","SPLIT",FACE,{"disambiguationData":[TD([subQ48])],"derivedFrom":makeQuery(id+"F3.boolean.opBoolean","SPLIT",FACE,{"disambiguationData":[TD([subQ48])],"derivedFrom":makeQuery(id+"F1.opExtrude","CAP_FACE",FACE,{"disambiguationData":[OSD([subQ47])],"isStart":false})})});}
            var sketch = newSketch(context, id + "F6", { "sketchPlane" : qUnion([Q0])});
            skLineSegment(sketch, "E75", {"start": v(-55.54, 23.79) * mm, "end": v(-58.41, 16.33) * mm});
            skArc(sketch, "E76", {"start": v(-59.5, 14.96) * mm, "mid": v(-58.85, 15.56) * mm, "end": v(-58.41, 16.33) * mm});
            skArc(sketch, "E77", {"start": v(-60.75, 14.96) * mm, "mid": v(-60.12, 14.84) * mm, "end": v(-59.5, 14.96) * mm});
            skLineSegment(sketch, "E78", {"start": v(-60.75, 14.96) * mm, "end": v(-61.15, 15.18) * mm});
            skLineSegment(sketch, "E79", {"start": v(-61.15, 15.18) * mm, "end": v(-61.04, 14.84) * mm});
            skArc(sketch, "E80", {"start": v(-61.1, 12.3) * mm, "mid": v(-60.85, 13.57) * mm, "end": v(-61.04, 14.84) * mm});
            skArc(sketch, "E81", {"start": v(-60.26, 12.3) * mm, "mid": v(-60.68, 12.41) * mm, "end": v(-61.1, 12.3) * mm});
            skLineSegment(sketch, "E82", {"start": v(-55.81, 21.34) * mm, "end": v(-58.48, 13.3) * mm});
            skLineSegment(sketch, "E83", {"start": v(-55.81, 21.34) * mm, "end": v(-52.72, 13.3) * mm});
            skLineSegment(sketch, "E84", {"start": v(-55.54, 23.79) * mm, "end": v(-52.7, 16.33) * mm});
            skArc(sketch, "E85", {"start": v(-52.7, 16.33) * mm, "mid": v(-52.38, 15.8) * mm, "end": v(-51.92, 15.38) * mm});
            skArc(sketch, "E86", {"start": v(-51.92, 15.38) * mm, "mid": v(-51, 15.02) * mm, "end": v(-50.01, 15.2) * mm});
            skLineSegment(sketch, "E87", {"start": v(-50.01, 15.2) * mm, "end": v(-50.17, 14.77) * mm});
            skArc(sketch, "E88", {"start": v(-50.17, 14.77) * mm, "mid": v(-50.36, 13.54) * mm, "end": v(-50.1, 12.32) * mm});
            skArc(sketch, "E89", {"start": v(-58.48, 13.3) * mm, "mid": v(-58.5, 12.12) * mm, "end": v(-57.87, 11.13) * mm});
            skArc(sketch, "E90", {"start": v(-57.87, 11.13) * mm, "mid": v(-56.97, 10.53) * mm, "end": v(-55.96, 10.15) * mm});
            skArc(sketch, "E91", {"start": v(-52.72, 11.77) * mm, "mid": v(-52.57, 12.53) * mm, "end": v(-52.72, 13.3) * mm});
            skArc(sketch, "E92", {"start": v(-55.22, 10.16) * mm, "mid": v(-53.8, 10.72) * mm, "end": v(-52.72, 11.77) * mm});
            skArc(sketch, "E93", {"start": v(-50.1, 12.32) * mm, "mid": v(-50.48, 12.43) * mm, "end": v(-50.86, 12.32) * mm});
            skArc(sketch, "E94", {"start": v(-59.82, 11.93) * mm, "mid": v(-60.03, 12.12) * mm, "end": v(-60.26, 12.3) * mm});
            skLineSegment(sketch, "E95", {"start": v(-61.32, 12.18) * mm, "end": v(-60.4, 11.2) * mm});
            skLineSegment(sketch, "E96", {"start": v(-60.4, 11.2) * mm, "end": v(-59.73, 10.66) * mm});
            skLineSegment(sketch, "E97", {"start": v(-59.73, 10.66) * mm, "end": v(-59.35, 10.4) * mm});
            skLineSegment(sketch, "E98", {"start": v(-59.35, 10.4) * mm, "end": v(-58.92, 10.12) * mm});
            skLineSegment(sketch, "E99", {"start": v(-58.92, 10.12) * mm, "end": v(-58.34, 9.89) * mm});
            skLineSegment(sketch, "E100", {"start": v(-58.34, 9.89) * mm, "end": v(-57.88, 9.72) * mm});
            skLineSegment(sketch, "E101", {"start": v(-57.88, 9.72) * mm, "end": v(-57.48, 9.59) * mm});
            skArc(sketch, "E102", {"start": v(-56.12, 9.7) * mm, "mid": v(-55.8, 9.98) * mm, "end": v(-55.63, 10.37) * mm});
            skArc(sketch, "E103", {"start": v(-55.63, 10.37) * mm, "mid": v(-55.54, 10.05) * mm, "end": v(-55.29, 9.83) * mm});
            skArc(sketch, "E104", {"start": v(-55.29, 9.83) * mm, "mid": v(-54.82, 9.6) * mm, "end": v(-54.3, 9.59) * mm});
            skLineSegment(sketch, "E105", {"start": v(-54.3, 9.59) * mm, "end": v(-53.6, 9.67) * mm});
            skLineSegment(sketch, "E106", {"start": v(-53.6, 9.67) * mm, "end": v(-53.09, 9.82) * mm});
            skLineSegment(sketch, "E107", {"start": v(-53.09, 9.82) * mm, "end": v(-52.5, 10.06) * mm});
            skLineSegment(sketch, "E108", {"start": v(-52.5, 10.06) * mm, "end": v(-51.96, 10.38) * mm});
            skLineSegment(sketch, "E109", {"start": v(-51.96, 10.38) * mm, "end": v(-51.38, 10.76) * mm});
            skLineSegment(sketch, "E110", {"start": v(-51.38, 10.76) * mm, "end": v(-49.9, 12.15) * mm});
            skLineSegment(sketch, "E111", {"start": v(-49.9, 12.15) * mm, "end": v(-50.17, 11.7) * mm});
            skLineSegment(sketch, "E112", {"start": v(-50.17, 11.7) * mm, "end": v(-50.43, 11.4) * mm});
            skLineSegment(sketch, "E113", {"start": v(-50.43, 11.4) * mm, "end": v(-50.85, 10.98) * mm});
            skLineSegment(sketch, "E114", {"start": v(-50.85, 10.98) * mm, "end": v(-51.96, 10.07) * mm});
            skLineSegment(sketch, "E115", {"start": v(-61.32, 12.18) * mm, "end": v(-60.88, 11.47) * mm});
            skLineSegment(sketch, "E116", {"start": v(-60.88, 11.47) * mm, "end": v(-60.06, 10.68) * mm});
            skLineSegment(sketch, "E117", {"start": v(-60.06, 10.68) * mm, "end": v(-59.18, 10) * mm});
            skArc(sketch, "E118", {"start": v(-59.18, 10) * mm, "mid": v(-55.56, 8.92) * mm, "end": v(-51.96, 10.07) * mm});
            skArc(sketch, "E119", {"start": v(-59.82, 11.93) * mm, "mid": v(-59.44, 11.58) * mm, "end": v(-59, 11.3) * mm});
            skArc(sketch, "E120", {"start": v(-58.13, 10.76) * mm, "mid": v(-58.56, 11.04) * mm, "end": v(-59, 11.3) * mm});
            skLineSegment(sketch, "E121", {"start": v(-58.13, 10.76) * mm, "end": v(-57.2, 10.4) * mm});
            skLineSegment(sketch, "E122", {"start": v(-57.2, 10.4) * mm, "end": v(-56.18, 10.1) * mm});
            skLineSegment(sketch, "E123", {"start": v(-56.18, 10.1) * mm, "end": v(-55.96, 10.15) * mm});
            skLineSegment(sketch, "E124", {"start": v(-55.22, 10.16) * mm, "end": v(-55.22, 10.09) * mm});
            skLineSegment(sketch, "E125", {"start": v(-55.22, 10.09) * mm, "end": v(-55.08, 10.09) * mm});
            skLineSegment(sketch, "E126", {"start": v(-55.08, 10.09) * mm, "end": v(-54.93, 10.12) * mm});
            skArc(sketch, "E127", {"start": v(-54.93, 10.12) * mm, "mid": v(-54.13, 10.33) * mm, "end": v(-53.38, 10.64) * mm});
            skArc(sketch, "E128", {"start": v(-53.38, 10.64) * mm, "mid": v(-52.8, 10.88) * mm, "end": v(-52.27, 11.19) * mm});
            skArc(sketch, "E129", {"start": v(-52.27, 11.19) * mm, "mid": v(-51.81, 11.54) * mm, "end": v(-51.38, 11.91) * mm});
            skArc(sketch, "E130", {"start": v(-57.48, 9.59) * mm, "mid": v(-56.79, 9.5) * mm, "end": v(-56.12, 9.7) * mm});
            skArc(sketch, "E131", {"start": v(-50.86, 12.32) * mm, "mid": v(-51.14, 12.14) * mm, "end": v(-51.38, 11.91) * mm});
            skSolve(sketch);
        }
        {
            var Q0;
            Q0=makeQuery(id+"F6.imprint","IMPRINT",FACE,{"disambiguationData":[TD([[makeQuery(id+"F6.imprint","IMPRINT",EDGE,{"derivedFrom":sQuery(id+"F6.wireOp",EDGE,"E75")}),1.0]])]});
            var Q1;
            Q1=makeQuery(id+"F6.imprint","IMPRINT",FACE,{"disambiguationData":[TD([[makeQuery(id+"F6.imprint","IMPRINT",EDGE,{"derivedFrom":sQuery(id+"F6.wireOp",EDGE,"E95")}),-1.0]])]});
            extrude(context, id + "F7", {"entities" : qUnion([Q0, Q1]), "operationType" : NewBodyOperationType.ADD, "depth" : 3.17 * mm, "offsetDistance" : 25.4 * mm});
        }
        {
            var Q0;
            {var subQ47=sQuery(id+"F0.wireOp",EDGE,"E0");var subQ48=makeQuery(id+"F1.opExtrude","SWEPT_FACE",FACE,{"disambiguationData":[OSD([subQ47])]});Q0=makeQuery(id+"F5.boolean.opBoolean","SPLIT",FACE,{"disambiguationData":[TD([subQ48])],"derivedFrom":makeQuery(id+"F3.boolean.opBoolean","SPLIT",FACE,{"disambiguationData":[TD([subQ48])],"derivedFrom":makeQuery(id+"F1.opExtrude","CAP_FACE",FACE,{"disambiguationData":[OSD([subQ47])],"isStart":false})})});}
            var sketch = newSketch(context, id + "F8", { "sketchPlane" : qUnion([Q0])});
            skLineSegment(sketch, "E132", {"start": v(-35.26, 18.31) * mm, "end": v(-33.3, 18.05) * mm});
            skLineSegment(sketch, "E133", {"start": v(-33.3, 18.05) * mm, "end": v(-32.61, 14.19) * mm});
            skLineSegment(sketch, "E134", {"start": v(-32.61, 14.19) * mm, "end": v(-41.17, 9.67) * mm});
            skLineSegment(sketch, "E135", {"start": v(-41.17, 9.67) * mm, "end": v(-38.66, 12.27) * mm});
            skLineSegment(sketch, "E136", {"start": v(-38.66, 12.27) * mm, "end": v(-35.4, 15.58) * mm});
            skLineSegment(sketch, "E137", {"start": v(-35.4, 15.58) * mm, "end": v(-36, 16.17) * mm});
            skLineSegment(sketch, "E138", {"start": v(-36, 16.17) * mm, "end": v(-37.88, 14.43) * mm});
            skLineSegment(sketch, "E139", {"start": v(-37.88, 14.43) * mm, "end": v(-39.75, 14.77) * mm});
            skLineSegment(sketch, "E140", {"start": v(-39.75, 14.77) * mm, "end": v(-40.45, 18.6) * mm});
            skLineSegment(sketch, "E141", {"start": v(-40.45, 18.6) * mm, "end": v(-31.69, 23.1) * mm});
            skLineSegment(sketch, "E142", {"start": v(-31.69, 23.1) * mm, "end": v(-37.8, 17.11) * mm});
            skLineSegment(sketch, "E143", {"start": v(-37.8, 17.11) * mm, "end": v(-37.2, 16.51) * mm});
            skLineSegment(sketch, "E144", {"start": v(-37.2, 16.51) * mm, "end": v(-35.26, 18.31) * mm});
            skLineSegment(sketch, "E145", {"start": v(-40.1, 14.7) * mm, "end": v(-41.03, 19.5) * mm});
            skArc(sketch, "E146", {"start": v(-41.03, 19.5) * mm, "mid": v(-41.73, 18.37) * mm, "end": v(-41.99, 17.07) * mm});
            skArc(sketch, "E147", {"start": v(-41.99, 17.07) * mm, "mid": v(-42.02, 16.03) * mm, "end": v(-41.82, 15) * mm});
            skLineSegment(sketch, "E148", {"start": v(-40.1, 14.7) * mm, "end": v(-41.82, 15) * mm});
            skCircle(sketch, "E149", {"center": v(-40.85, 15.27) * mm, "radius": 0.2 * mm});
            skCircle(sketch, "E150", {"center": v(-32.82, 13.07) * mm, "radius": 0.2 * mm});
            skCircle(sketch, "E151", {"center": v(-39.07, 13.78) * mm, "radius": 0.22 * mm});
            skCircle(sketch, "E152", {"center": v(-33.98, 19.03) * mm, "radius": 0.25 * mm});
            skCircle(sketch, "E153", {"center": v(-32.23, 17.44) * mm, "radius": 0.23 * mm});
            skCircle(sketch, "E154", {"center": v(-40.31, 19.58) * mm, "radius": 0.2 * mm});
            skLineSegment(sketch, "E155", {"start": v(-38.02, 14.05) * mm, "end": v(-41.72, 14.75) * mm});
            skLineSegment(sketch, "E156", {"start": v(-38.02, 14.05) * mm, "end": v(-39.99, 12.12) * mm});
            skArc(sketch, "E157", {"start": v(-41.72, 14.75) * mm, "mid": v(-41.07, 13.29) * mm, "end": v(-39.99, 12.12) * mm});
            skLineSegment(sketch, "E158", {"start": v(-32.4, 13.88) * mm, "end": v(-37.6, 11.14) * mm});
            skLineSegment(sketch, "E159", {"start": v(-32.4, 13.88) * mm, "end": v(-32.23, 12.96) * mm});
            skArc(sketch, "E160", {"start": v(-33.54, 11.74) * mm, "mid": v(-32.82, 12.28) * mm, "end": v(-32.23, 12.96) * mm});
            skArc(sketch, "E161", {"start": v(-37.6, 11.14) * mm, "mid": v(-35.5, 10.97) * mm, "end": v(-33.54, 11.74) * mm});
            skLineSegment(sketch, "E162", {"start": v(-33, 18.15) * mm, "end": v(-32.1, 13.33) * mm});
            skLineSegment(sketch, "E163", {"start": v(-33, 18.15) * mm, "end": v(-31.2, 17.82) * mm});
            skArc(sketch, "E164", {"start": v(-32.1, 13.33) * mm, "mid": v(-31.17, 15.48) * mm, "end": v(-31.2, 17.82) * mm});
            skLineSegment(sketch, "E165", {"start": v(-31.45, 18.02) * mm, "end": v(-35.1, 18.69) * mm});
            skLineSegment(sketch, "E166", {"start": v(-35.1, 18.69) * mm, "end": v(-33.07, 20.53) * mm});
            skArc(sketch, "E167", {"start": v(-31.45, 18.02) * mm, "mid": v(-32.01, 19.44) * mm, "end": v(-33.07, 20.53) * mm});
            skLineSegment(sketch, "E168", {"start": v(-40.69, 18.9) * mm, "end": v(-40.85, 19.75) * mm});
            skLineSegment(sketch, "E169", {"start": v(-40.69, 18.9) * mm, "end": v(-35.47, 21.59) * mm});
            skArc(sketch, "E170", {"start": v(-35.47, 21.59) * mm, "mid": v(-36.51, 21.8) * mm, "end": v(-37.58, 21.74) * mm});
            skArc(sketch, "E171", {"start": v(-37.58, 21.74) * mm, "mid": v(-39.37, 21) * mm, "end": v(-40.85, 19.75) * mm});
            skArc(sketch, "E172", {"start": v(-38.84, 10.9) * mm, "mid": v(-31.32, 13.66) * mm, "end": v(-33.44, 21.39) * mm});
            skArc(sketch, "E173", {"start": v(-34.27, 21.77) * mm, "mid": v(-41.89, 19.02) * mm, "end": v(-39.66, 11.24) * mm});
            skLineSegment(sketch, "E174", {"start": v(-38.76, 10.87) * mm, "end": v(-41.59, 9.28) * mm});
            skLineSegment(sketch, "E175", {"start": v(-41.59, 9.28) * mm, "end": v(-39.88, 11.38) * mm});
            skLineSegment(sketch, "E176", {"start": v(-34.44, 21.84) * mm, "end": v(-31.43, 23.33) * mm});
            skLineSegment(sketch, "E177", {"start": v(-31.43, 23.33) * mm, "end": v(-33.34, 21.32) * mm});
            skSolve(sketch);
        }
        {
            var Q0;
            Q0=makeQuery(id+"F8.imprint","IMPRINT",FACE,{"disambiguationData":[TD([[makeQuery(id+"F8.imprint","IMPRINT",EDGE,{"derivedFrom":sQuery(id+"F8.wireOp",EDGE,"E132")}),1.0]])]});
            var Q1;
            {var subQ3=sQuery(id+"F8.wireOp",EDGE,"E136");Q1=makeQuery(id+"F8.imprint","IMPRINT",FACE,{"disambiguationData":[TD([[makeQuery(id+"F8.imprint","IMPRINT",EDGE,{"derivedFrom":subQ3}),1.0]])]});}
            var Q2;
            Q2=makeQuery(id+"F8.imprint","IMPRINT",FACE,{"disambiguationData":[TD([[makeQuery(id+"F8.imprint","IMPRINT",EDGE,{"derivedFrom":sQuery(id+"F8.wireOp",EDGE,"E154")}),1.0]])]});
            var Q3;
            Q3=makeQuery(id+"F8.imprint","IMPRINT",FACE,{"disambiguationData":[TD([[makeQuery(id+"F8.imprint","IMPRINT",EDGE,{"derivedFrom":sQuery(id+"F8.wireOp",EDGE,"E149")}),1.0]])]});
            var Q4;
            Q4=makeQuery(id+"F8.imprint","IMPRINT",FACE,{"disambiguationData":[TD([[makeQuery(id+"F8.imprint","IMPRINT",EDGE,{"derivedFrom":sQuery(id+"F8.wireOp",EDGE,"E151")}),1.0]])]});
            var Q5;
            Q5=makeQuery(id+"F8.imprint","IMPRINT",FACE,{"disambiguationData":[TD([[makeQuery(id+"F8.imprint","IMPRINT",EDGE,{"derivedFrom":sQuery(id+"F8.wireOp",EDGE,"E153")}),1.0]])]});
            var Q6;
            Q6=makeQuery(id+"F8.imprint","IMPRINT",FACE,{"disambiguationData":[TD([[makeQuery(id+"F8.imprint","IMPRINT",EDGE,{"derivedFrom":sQuery(id+"F8.wireOp",EDGE,"E152")}),1.0]])]});
            var Q7;
            Q7=makeQuery(id+"F8.imprint","IMPRINT",FACE,{"disambiguationData":[TD([[makeQuery(id+"F8.imprint","IMPRINT",EDGE,{"derivedFrom":sQuery(id+"F8.wireOp",EDGE,"E150")}),1.0]])]});
            var Q8;
            {var subQ8=sQuery(id+"F8.wireOp",EDGE,"E176");Q8=makeQuery(id+"F8.imprint","IMPRINT",FACE,{"disambiguationData":[TD([[makeQuery(id+"F8.imprint","IMPRINT",EDGE,{"derivedFrom":subQ8}),-1.0]])]});}
            var Q9;
            {var subQ7=sQuery(id+"F8.wireOp",EDGE,"E174");Q9=makeQuery(id+"F8.imprint","IMPRINT",FACE,{"disambiguationData":[TD([[makeQuery(id+"F8.imprint","IMPRINT",EDGE,{"derivedFrom":subQ7}),-1.0]])]});}
            extrude(context, id + "F9", {"entities" : qUnion([Q0, Q1, Q2, Q3, Q4, Q5, Q6, Q7, Q8, Q9]), "operationType" : NewBodyOperationType.REMOVE, "oppositeDirection" : true, "depth" : 3.17 * mm, "offsetDistance" : 25.4 * mm});
        }
    });
